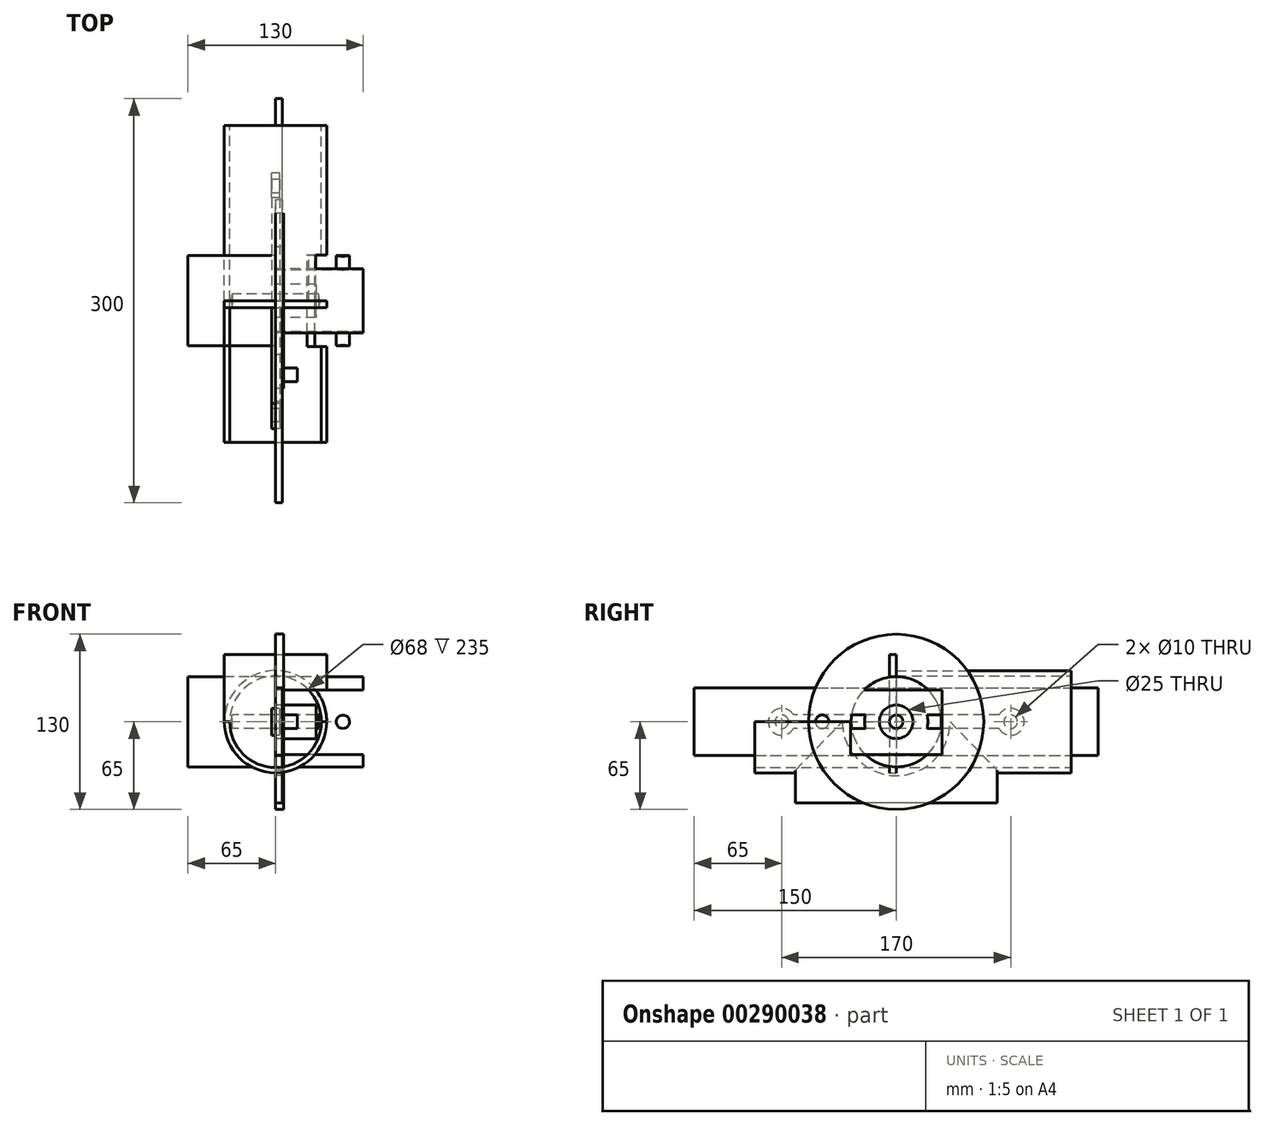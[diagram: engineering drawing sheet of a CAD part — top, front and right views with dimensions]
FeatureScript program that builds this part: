
annotation { "Feature Type Name" : "Feature", "Feature Type Description" : "" }
export const myFeature = defineFeature(function(context is Context, id is Id, definition is map)
    precondition{}
    {
        {
            var Q0;
            Q0=qCreatedBy(makeId("Front.planeOp"),FACE);
            var sketch = newSketch(context, id + "F0", { "sketchPlane" : qUnion([Q0])});
            skCircle(sketch, "E0", {"center": v(0, 0) * mm, "radius": 34 * mm});
            skCircle(sketch, "E1", {"center": v(0, 0) * mm, "radius": 38 * mm});
            skLineSegment(sketch, "E2", {"start": v(-38, 0) * mm, "end": v(-34, 0) * mm});
            skLineSegment(sketch, "E3", {"start": v(34, 0) * mm, "end": v(38, 0) * mm});
            skLineSegment(sketch, "E4.bottom", {"start": v(-34, 0) * mm, "end": v(-38, 0) * mm});
            skLineSegment(sketch, "E4.left", {"start": v(-34, 0) * mm, "end": v(-34, 0) * mm});
            skLineSegment(sketch, "E4.right", {"start": v(-38, 0) * mm, "end": v(-38, 0) * mm});
            skSolve(sketch);
        }
        {
            var Q0;
            {var subQ0=sQuery(id+"F0.wireOp",EDGE,"E3");Q0=makeQuery(id+"F0.imprint","IMPRINT",FACE,{"disambiguationData":[TD([[makeQuery(id+"F0.imprint","IMPRINT",EDGE,{"derivedFrom":subQ0}),-1.0]])]});}
            extrude(context, id + "F1", {"entities" : qUnion([Q0]), "flatOperationType" : FlatOperationType.REMOVE, "offsetDistance" : 25 * mm, "depth" : 105 * mm, "domain" : OperationDomain.MODEL});
        }
        {
            var Q0;
            Q0 = qSketchRegion(id + "F0", true);
            extrude(context, id + "F2", {"entities" : qUnion([Q0]), "operationType" : NewBodyOperationType.ADD, "flatOperationType" : FlatOperationType.REMOVE, "oppositeDirection" : true, "offsetDistance" : 25 * mm, "depth" : 130 * mm, "domain" : OperationDomain.MODEL});
        }
        {
            var Q0;
            Q0=qCreatedBy(makeId("Front.planeOp"),FACE);
            var sketch = newSketch(context, id + "F3", { "sketchPlane" : qUnion([Q0])});
            skCircle(sketch, "E5", {"center": v(0, 0) * mm, "radius": 38 * mm});
            skLineSegment(sketch, "E6.bottom", {"start": v(-38, 0) * mm, "end": v(38, 0) * mm});
            skLineSegment(sketch, "E6.top", {"start": v(-38, 50) * mm, "end": v(38, 50) * mm});
            skLineSegment(sketch, "E6.left", {"start": v(-38, 0) * mm, "end": v(-38, 50) * mm});
            skLineSegment(sketch, "E6.right", {"start": v(38, 0) * mm, "end": v(38, 50) * mm});
            skSolve(sketch);
        }
        {
            var Q0;
            {var subQ0=sQuery(id+"F3.wireOp",EDGE,"E6.right");Q0=makeQuery(id+"F3.imprint","IMPRINT",FACE,{"disambiguationData":[TD([[makeQuery(id+"F3.imprint","IMPRINT",EDGE,{"derivedFrom":subQ0}),1.0]])]});}
            var Q1;
            {var subQ0=sQuery(id+"F3.wireOp",EDGE,"E6.left");Q1=makeQuery(id+"F3.imprint","IMPRINT",FACE,{"disambiguationData":[TD([[makeQuery(id+"F3.imprint","IMPRINT",EDGE,{"derivedFrom":subQ0}),-1.0]])]});}
            var Q2;
            {var subQ0=sQuery(id+"F3.wireOp",EDGE,"E6.bottom");Q2=makeQuery(id+"F3.imprint","IMPRINT",FACE,{"disambiguationData":[TD([[makeQuery(id+"F3.imprint","IMPRINT",EDGE,{"derivedFrom":subQ0}),-1.0]])]});}
            var Q3;
            {var subQ0=sQuery(id+"F3.wireOp",EDGE,"E6.bottom");Q3=makeQuery(id+"F3.imprint","IMPRINT",FACE,{"disambiguationData":[TD([[makeQuery(id+"F3.imprint","IMPRINT",EDGE,{"derivedFrom":subQ0}),1.0]])]});}
            extrude(context, id + "F4", {"entities" : qUnion([Q0, Q1, Q2, Q3]), "depth" : 5 * mm});
        }
        {
            var Q0;
            Q0=qCreatedBy(makeId("Front.planeOp"),FACE);
            var sketch = newSketch(context, id + "F5", { "sketchPlane" : qUnion([Q0])});
            skLineSegment(sketch, "E7.right", {"start": v(21153.36, 49.49) * mm, "end": v(21153.36, -241.49) * mm});
            skLineSegment(sketch, "E8.bottom", {"start": v(65, 33.5) * mm, "end": v(-65, 33.5) * mm});
            skLineSegment(sketch, "E8.top", {"start": v(65, -33.5) * mm, "end": v(-65, -33.5) * mm});
            skLineSegment(sketch, "E8.left", {"start": v(65, 33.5) * mm, "end": v(65, -33.5) * mm});
            skLineSegment(sketch, "E8.right", {"start": v(-65, 33.5) * mm, "end": v(-65, -33.5) * mm});
            skPoint(sketch, "E8.middle", {"position": v(0, 0) * mm});
            skLineSegment(sketch, "E9", {"start": v(0, 33.5) * mm, "end": v(0, -33.5) * mm});
            skLineSegment(sketch, "E10", {"start": v(-65, 0) * mm, "end": v(65, 0) * mm});
            skLineSegment(sketch, "E11.bottom", {"start": v(65, 23.5) * mm, "end": v(0, 23.5) * mm});
            skLineSegment(sketch, "E11.top", {"start": v(65, -24.5) * mm, "end": v(0, -24.5) * mm});
            skLineSegment(sketch, "E11.left", {"start": v(65, 23.5) * mm, "end": v(65, -24.5) * mm});
            skLineSegment(sketch, "E11.right", {"start": v(0, 23.5) * mm, "end": v(0, -24.5) * mm});
            skPoint(sketch, "E12", {"position": v(50, 0) * mm});
            skCircle(sketch, "E13", {"center": v(50, 0) * mm, "radius": 5 * mm});
            skSolve(sketch);
        }
        {
            var Q0;
            {var subQ5=sQuery(id+"F5.wireOp",EDGE,"E11.bottom");Q0=makeQuery(id+"F5.imprint","IMPRINT",FACE,{"disambiguationData":[TD([[makeQuery(id+"F5.imprint","IMPRINT",EDGE,{"derivedFrom":subQ5}),-1.0]])]});}
            var Q1;
            {var subQ1=sQuery(id+"F5.wireOp",EDGE,"E8.right");var subQ6=sQuery(id+"F5.wireOp",EDGE,"E8.bottom");var subQ9=makeQuery(id+"F5.imprint","INTERSECT",VERTEX,{"derivedFrom":[subQ6,subQ1]});Q1=makeQuery(id+"F5.imprint","IMPRINT",FACE,{"disambiguationData":[TD([[makeQuery(id+"F5.imprint","IMPRINT",EDGE,{"disambiguationData":[TD([[subQ9,1.0]])],"derivedFrom":subQ6}),1.0]])]});}
            var Q2;
            Q2=sQuery(id+"F5.wireOp",EDGE,"E10");
            revolve(context, id + "F6", {"entities" : qUnion([Q0, Q1]), "axis" : qUnion([Q2]), "revolveType" : RevolveType.FULL});
        }
        {
            var Q0;
            {var subQ0=sQuery(id+"F5.wireOp",EDGE,"E13");var subQ1=sQuery(id+"F5.wireOp",EDGE,"E10");var subQ2=makeQuery(id+"F5.imprint","INTERSECT",VERTEX,{"disambiguationData":[OD(0.0)],"derivedFrom":[subQ1,subQ0]});Q0=makeQuery(id+"F5.imprint","IMPRINT",FACE,{"disambiguationData":[TD([[makeQuery(id+"F5.imprint","IMPRINT",EDGE,{"disambiguationData":[TD([[subQ2,-1.0]])],"derivedFrom":subQ1}),-1.0]])]});}
            var Q1;
            {var subQ0=sQuery(id+"F5.wireOp",EDGE,"E13");var subQ1=sQuery(id+"F5.wireOp",EDGE,"E10");var subQ2=makeQuery(id+"F5.imprint","INTERSECT",VERTEX,{"disambiguationData":[OD(0.0)],"derivedFrom":[subQ1,subQ0]});Q1=makeQuery(id+"F5.imprint","IMPRINT",FACE,{"disambiguationData":[TD([[makeQuery(id+"F5.imprint","IMPRINT",EDGE,{"disambiguationData":[TD([[subQ2,-1.0]])],"derivedFrom":subQ1}),1.0]])]});}
            var Q2;
            Q2 = qSketchRegion(id + "F11", true);
            extrude(context, id + "F7", {"entities" : qUnion([Q0, Q1, Q2]), "operationType" : NewBodyOperationType.REMOVE, "oppositeDirection" : true, "depth" : 68 * mm, "symmetric" : true});
        }
        {
            var Q0;
            Q0=qCreatedBy(makeId("Right.planeOp"),FACE);
            var sketch = newSketch(context, id + "F8", { "sketchPlane" : qUnion([Q0])});
            skCircle(sketch, "E14", {"center": v(0, 0) * mm, "radius": 65 * mm});
            skCircle(sketch, "E15", {"center": v(0, 0) * mm, "radius": 12.5 * mm});
            skLineSegment(sketch, "E16", {"start": v(65, 0) * mm, "end": v(-65, 0) * mm});
            skCircle(sketch, "E17", {"center": v(-55, 0) * mm, "radius": 5 * mm});
            skSolve(sketch);
        }
        {
            var Q0;
            Q0 = qSketchRegion(id + "F8", true);
            extrude(context, id + "F9", {"entities" : qUnion([Q0]), "flatOperationType" : FlatOperationType.REMOVE, "offsetDistance" : 25 * mm, "depth" : 6 * mm, "domain" : OperationDomain.MODEL});
        }
        {
            var Q0;
            {var subQ0=sQuery(id+"F8.wireOp",EDGE,"E17");var subQ1=sQuery(id+"F8.wireOp",EDGE,"E16");var subQ2=makeQuery(id+"F8.imprint","INTERSECT",VERTEX,{"disambiguationData":[OD(0.0)],"derivedFrom":[subQ1,subQ0]});Q0=makeQuery(id+"F8.imprint","IMPRINT",FACE,{"disambiguationData":[TD([[makeQuery(id+"F8.imprint","IMPRINT",EDGE,{"disambiguationData":[TD([[subQ2,-1.0]])],"derivedFrom":subQ1}),1.0]])]});}
            var Q1;
            {var subQ0=sQuery(id+"F8.wireOp",EDGE,"E17");var subQ1=sQuery(id+"F8.wireOp",EDGE,"E16");var subQ2=makeQuery(id+"F8.imprint","INTERSECT",VERTEX,{"disambiguationData":[OD(0.0)],"derivedFrom":[subQ1,subQ0]});Q1=makeQuery(id+"F8.imprint","IMPRINT",FACE,{"disambiguationData":[TD([[makeQuery(id+"F8.imprint","IMPRINT",EDGE,{"disambiguationData":[TD([[subQ2,-1.0]])],"derivedFrom":subQ1}),-1.0]])]});}
            extrude(context, id + "F10", {"entities" : qUnion([Q0, Q1]), "operationType" : NewBodyOperationType.ADD, "depth" : 16 * mm});
        }
        {
            var Q0;
            Q0=qCreatedBy(makeId("Right.planeOp"),FACE);
            var sketch = newSketch(context, id + "F11", { "sketchPlane" : qUnion([Q0])});
            skCircle(sketch, "E18", {"center": v(0, 0) * mm, "radius": 5 * mm});
            skSolve(sketch);
        }
        {
            var Q0;
            Q0=makeQuery(id+"F11.imprint","IMPRINT",FACE,{"disambiguationData":[TD([[makeQuery(id+"F11.imprint","IMPRINT",EDGE,{"derivedFrom":sQuery(id+"F11.wireOp",EDGE,"E18")}),1.0]])]});
            extrude(context, id + "F12", {"entities" : qUnion([Q0]), "depth" : 66 * mm, "symmetric" : true});
        }
        {
            var Q0;
            Q0=makeQuery(id+"F12.opExtrude","CAP_EDGE",EDGE,{"disambiguationData":[OSD([sQuery(id+"F11.wireOp",EDGE,"E18")])],"isStart":false});
            chamfer(context, id + "F13", {"entities" : qUnion([Q0]), "chamferType" : ChamferType.TWO_OFFSETS, "width1" : 5 * mm, "oppositeDirection" : false, "width2" : 1 * mm, "tangentPropagation" : true});
        }
        {
            var Q0;
            Q0=makeQuery(id+"F12.opExtrude","CAP_FACE",FACE,{"disambiguationData":[OSD([sQuery(id+"F11.wireOp",EDGE,"E18")])],"isStart":true});
            chamfer(context, id + "F14", {"entities" : qUnion([Q0]), "chamferType" : ChamferType.TWO_OFFSETS, "width1" : 1 * mm, "oppositeDirection" : false, "width2" : 5 * mm, "tangentPropagation" : true});
        }
        {
            var Q0;
            Q0=qCreatedBy(makeId("Right.planeOp"),FACE);
            var sketch = newSketch(context, id + "F15", { "sketchPlane" : qUnion([Q0])});
            skLineSegment(sketch, "E19.bottom", {"start": v(85, 5) * mm, "end": v(-85, 5) * mm});
            skLineSegment(sketch, "E19.top", {"start": v(85, -5) * mm, "end": v(-85, -5) * mm});
            skLineSegment(sketch, "E19.left", {"start": v(85, 5) * mm, "end": v(85, -5) * mm});
            skLineSegment(sketch, "E19.right", {"start": v(-85, 5) * mm, "end": v(-85, -5) * mm});
            skPoint(sketch, "E19.middle", {"position": v(0, 0) * mm});
            skCircle(sketch, "E20", {"center": v(-85, 0) * mm, "radius": 10 * mm});
            skCircle(sketch, "E21", {"center": v(-85, 0) * mm, "radius": 5 * mm});
            skCircle(sketch, "E22", {"center": v(85, 0) * mm, "radius": 10 * mm});
            skCircle(sketch, "E23", {"center": v(85, 0) * mm, "radius": 5 * mm});
            skSolve(sketch);
        }
        {
            var Q0;
            {var subQ2=sQuery(id+"F15.wireOp",EDGE,"E19.bottom");var subQ4=sQuery(id+"F15.wireOp",EDGE,"E20");var subQ5=makeQuery(id+"F15.imprint","INTERSECT",VERTEX,{"derivedFrom":[subQ2,subQ4]});Q0=makeQuery(id+"F15.imprint","IMPRINT",FACE,{"disambiguationData":[TD([[makeQuery(id+"F15.imprint","IMPRINT",EDGE,{"disambiguationData":[TD([[subQ5,-1.0]])],"derivedFrom":subQ4}),1.0]])]});}
            var Q1;
            {var subQ2=sQuery(id+"F15.wireOp",EDGE,"E19.bottom");var subQ4=sQuery(id+"F15.wireOp",EDGE,"E20");var subQ5=makeQuery(id+"F15.imprint","INTERSECT",VERTEX,{"derivedFrom":[subQ2,subQ4]});Q1=makeQuery(id+"F15.imprint","IMPRINT",FACE,{"disambiguationData":[TD([[makeQuery(id+"F15.imprint","IMPRINT",EDGE,{"disambiguationData":[TD([[subQ5,1.0]])],"derivedFrom":subQ4}),1.0]])]});}
            var Q2;
            {var subQ0=sQuery(id+"F15.wireOp",EDGE,"E22");var subQ1=sQuery(id+"F15.wireOp",EDGE,"E19.bottom");var subQ2=makeQuery(id+"F15.imprint","INTERSECT",VERTEX,{"derivedFrom":[subQ1,subQ0]});Q2=makeQuery(id+"F15.imprint","IMPRINT",FACE,{"disambiguationData":[TD([[makeQuery(id+"F15.imprint","IMPRINT",EDGE,{"disambiguationData":[TD([[subQ2,-1.0]])],"derivedFrom":subQ1}),1.0]])]});}
            var Q3;
            {var subQ2=sQuery(id+"F15.wireOp",EDGE,"E19.bottom");var subQ4=sQuery(id+"F15.wireOp",EDGE,"E22");var subQ5=makeQuery(id+"F15.imprint","INTERSECT",VERTEX,{"derivedFrom":[subQ2,subQ4]});Q3=makeQuery(id+"F15.imprint","IMPRINT",FACE,{"disambiguationData":[TD([[makeQuery(id+"F15.imprint","IMPRINT",EDGE,{"disambiguationData":[TD([[subQ5,-1.0]])],"derivedFrom":subQ4}),1.0]])]});}
            var Q4;
            {var subQ2=sQuery(id+"F15.wireOp",EDGE,"E19.bottom");var subQ4=sQuery(id+"F15.wireOp",EDGE,"E22");var subQ5=makeQuery(id+"F15.imprint","INTERSECT",VERTEX,{"derivedFrom":[subQ2,subQ4]});Q4=makeQuery(id+"F15.imprint","IMPRINT",FACE,{"disambiguationData":[TD([[makeQuery(id+"F15.imprint","IMPRINT",EDGE,{"disambiguationData":[TD([[subQ5,1.0]])],"derivedFrom":subQ4}),1.0]])]});}
            extrude(context, id + "F16", {"entities" : qUnion([Q0, Q1, Q2, Q3, Q4]), "depth" : 6 * mm, "symmetric" : true});
        }
        {
            var Q0;
            Q0=qCreatedBy(makeId("Right.planeOp"),FACE);
            var sketch = newSketch(context, id + "F17", { "sketchPlane" : qUnion([Q0])});
            skCircle(sketch, "E24", {"center": v(0, 0) * mm, "radius": 12.5 * mm});
            skSolve(sketch);
        }
        {
            var Q0;
            Q0 = qSketchRegion(id + "F17", true);
            extrude(context, id + "F18", {"entities" : qUnion([Q0]), "depth" : 30 * mm});
        }
        {
            var Q0;
            Q0=qCreatedBy(makeId("Right.planeOp"),FACE);
            var sketch = newSketch(context, id + "F19", { "sketchPlane" : qUnion([Q0])});
            skLineSegment(sketch, "E25.bottom", {"start": v(-150, 25) * mm, "end": v(150, 25) * mm});
            skLineSegment(sketch, "E25.top", {"start": v(-150, -25) * mm, "end": v(150, -25) * mm});
            skLineSegment(sketch, "E25.left", {"start": v(-150, 25) * mm, "end": v(-150, -25) * mm});
            skLineSegment(sketch, "E25.right", {"start": v(150, 25) * mm, "end": v(150, -25) * mm});
            skPoint(sketch, "E25.middle", {"position": v(0, 0) * mm});
            skSolve(sketch);
        }
        {
            var Q0;
            Q0 = qSketchRegion(id + "F19", true);
            extrude(context, id + "F20", {"entities" : qUnion([Q0]), "depth" : 5 * mm});
        }
        {
            var Q0;
            Q0=qCreatedBy(makeId("Right.planeOp"),FACE);
            var sketch = newSketch(context, id + "F21", { "sketchPlane" : qUnion([Q0])});
            skCircle(sketch, "E26", {"center": v(0, 0) * mm, "radius": 40 * mm});
            skLineSegment(sketch, "E27.bottom", {"start": v(75, 0) * mm, "end": v(-75, 0) * mm});
            skLineSegment(sketch, "E27.top", {"start": v(75, -60.42) * mm, "end": v(-75, -60.42) * mm});
            skLineSegment(sketch, "E27.left", {"start": v(75, 0) * mm, "end": v(75, -60.42) * mm});
            skLineSegment(sketch, "E27.right", {"start": v(-75, 0) * mm, "end": v(-75, -60.42) * mm});
            skLineSegment(sketch, "E28", {"start": v(75, -36.12) * mm, "end": v(-75, -36.12) * mm});
            skLineSegment(sketch, "E29", {"start": v(-75, -36.12) * mm, "end": v(-40, 0) * mm});
            skLineSegment(sketch, "E30", {"start": v(-40, 0) * mm, "end": v(40, 0) * mm});
            skLineSegment(sketch, "E31", {"start": v(40, 0) * mm, "end": v(75, -36.12) * mm});
            skSolve(sketch);
        }
        {
            var Q0;
            {var subQ0=sQuery(id+"F21.wireOp",EDGE,"E31");Q0=makeQuery(id+"F21.imprint","IMPRINT",FACE,{"disambiguationData":[TD([[makeQuery(id+"F21.imprint","IMPRINT",EDGE,{"derivedFrom":subQ0}),-1.0]])]});}
            var Q1;
            {var subQ1=sQuery(id+"F21.wireOp",EDGE,"E27.top");Q1=makeQuery(id+"F21.imprint","IMPRINT",FACE,{"disambiguationData":[TD([[makeQuery(id+"F21.imprint","IMPRINT",EDGE,{"derivedFrom":subQ1}),-1.0]])]});}
            var Q2;
            {var subQ0=sQuery(id+"F21.wireOp",EDGE,"E29");Q2=makeQuery(id+"F21.imprint","IMPRINT",FACE,{"disambiguationData":[TD([[makeQuery(id+"F21.imprint","IMPRINT",EDGE,{"derivedFrom":subQ0}),-1.0]])]});}
            extrude(context, id + "F22", {"entities" : qUnion([Q0, Q1, Q2]), "depth" : 5 * mm});
        }
    });
